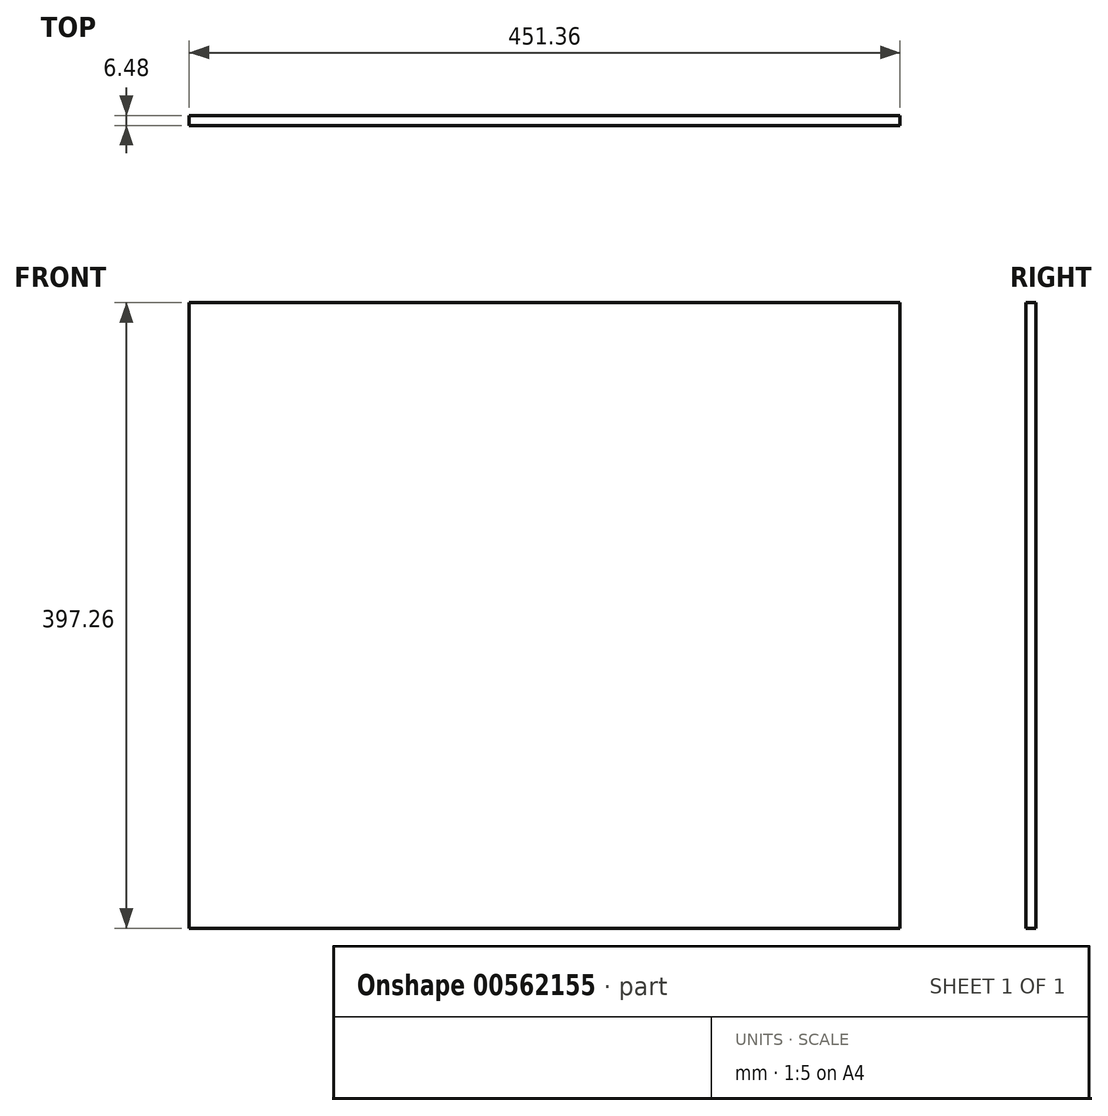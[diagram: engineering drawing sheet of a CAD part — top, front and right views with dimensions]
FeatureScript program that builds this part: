
annotation { "Feature Type Name" : "Feature", "Feature Type Description" : "" }
export const myFeature = defineFeature(function(context is Context, id is Id, definition is map)
    precondition{}
    {
        {
            var Q0;
            Q0=qCreatedBy(makeId("Front.planeOp"),FACE);
            var sketch = newSketch(context, id + "F0", { "sketchPlane" : qUnion([Q0])});
            skLineSegment(sketch, "E0.bottom", {"start": v(-261.72, 188.74) * mm, "end": v(189.64, 188.74) * mm});
            skLineSegment(sketch, "E0.top", {"start": v(-261.72, -208.52) * mm, "end": v(189.64, -208.52) * mm});
            skLineSegment(sketch, "E0.left", {"start": v(-261.72, 188.74) * mm, "end": v(-261.72, -208.52) * mm});
            skLineSegment(sketch, "E0.right", {"start": v(189.64, 188.74) * mm, "end": v(189.64, -208.52) * mm});
            skSolve(sketch);
        }
        {
            var Q0;
            Q0=makeQuery(id+"F0.imprint","IMPRINT",FACE,{"disambiguationData":[TD([[makeQuery(id+"F0.imprint","IMPRINT",EDGE,{"derivedFrom":sQuery(id+"F0.wireOp",EDGE,"E0.bottom")}),-1.0]])]});
            extrude(context, id + "F1", {"entities" : qUnion([Q0]), "depth" : 6.48 * mm, "offsetDistance" : 25.4 * mm});
        }
    });
